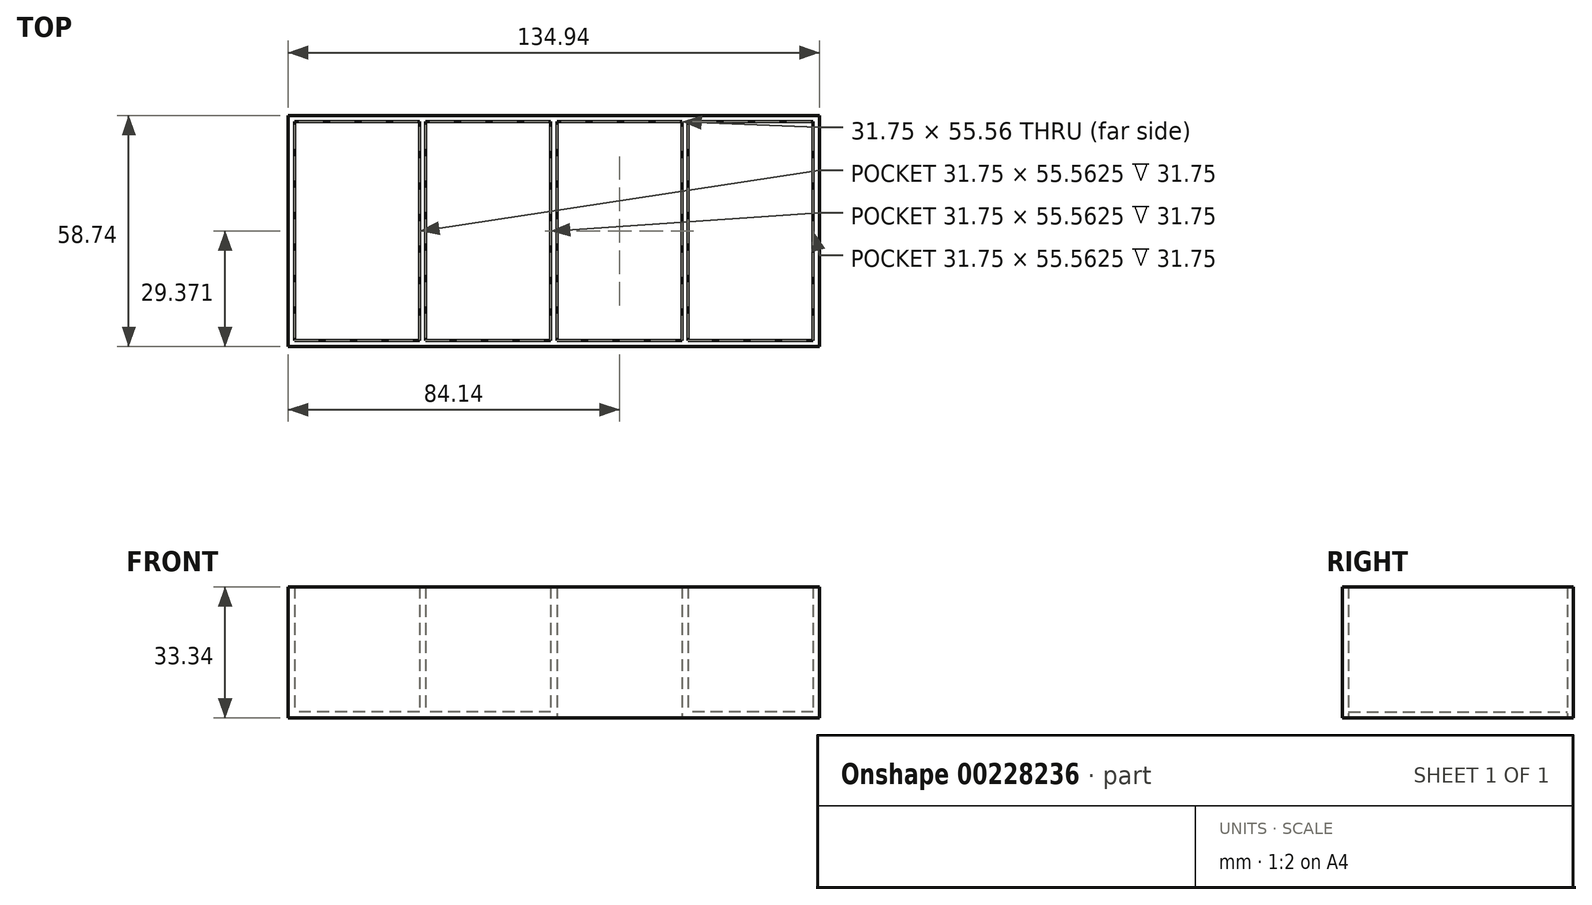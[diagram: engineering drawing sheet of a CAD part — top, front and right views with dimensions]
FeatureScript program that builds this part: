
annotation { "Feature Type Name" : "Feature", "Feature Type Description" : "" }
export const myFeature = defineFeature(function(context is Context, id is Id, definition is map)
    precondition{}
    {
        {
            var Q0;
            Q0=qCreatedBy(makeId("Top.planeOp"),FACE);
            var sketch = newSketch(context, id + "F0", { "sketchPlane" : qUnion([Q0])});
            skLineSegment(sketch, "E0.bottom", {"start": v(0, 0) * mm, "end": v(-31.75, 0) * mm});
            skLineSegment(sketch, "E0.top", {"start": v(0, 55.56) * mm, "end": v(-31.75, 55.56) * mm});
            skLineSegment(sketch, "E0.left", {"start": v(0, 0) * mm, "end": v(0, 55.56) * mm});
            skLineSegment(sketch, "E0.right", {"start": v(-31.75, 0) * mm, "end": v(-31.75, 55.56) * mm});
            skLineSegment(sketch, "E1.bottom", {"start": v(0, 0) * mm, "end": v(1.59, 0) * mm});
            skLineSegment(sketch, "E1.top", {"start": v(0, 55.56) * mm, "end": v(1.59, 55.56) * mm});
            skLineSegment(sketch, "E1.right", {"start": v(1.59, 0) * mm, "end": v(1.59, 55.56) * mm});
            skLineSegment(sketch, "E2.1.0.1", {"start": v(33.34, 55.56) * mm, "end": v(1.59, 55.56) * mm});
            skLineSegment(sketch, "E2.1.0.2", {"start": v(33.34, 0) * mm, "end": v(1.59, 0) * mm});
            skLineSegment(sketch, "E2.1.0.3", {"start": v(33.34, 0) * mm, "end": v(33.34, 55.56) * mm});
            skLineSegment(sketch, "E2.1.0.4", {"start": v(34.93, 0) * mm, "end": v(34.92, 55.56) * mm});
            skLineSegment(sketch, "E2.1.0.5", {"start": v(33.34, 0) * mm, "end": v(34.93, 0) * mm});
            skLineSegment(sketch, "E2.1.0.6", {"start": v(33.34, 55.56) * mm, "end": v(34.92, 55.56) * mm});
            skLineSegment(sketch, "E2.2.0.0", {"start": v(34.93, 0) * mm, "end": v(34.93, 55.56) * mm});
            skLineSegment(sketch, "E2.2.0.1", {"start": v(66.67, 55.56) * mm, "end": v(34.93, 55.56) * mm});
            skLineSegment(sketch, "E2.2.0.2", {"start": v(66.68, 0) * mm, "end": v(34.93, 0) * mm});
            skLineSegment(sketch, "E2.2.0.3", {"start": v(66.68, 0) * mm, "end": v(66.68, 55.56) * mm});
            skLineSegment(sketch, "E2.2.0.4", {"start": v(68.26, 0) * mm, "end": v(68.26, 55.56) * mm});
            skLineSegment(sketch, "E2.2.0.5", {"start": v(66.68, 0) * mm, "end": v(68.26, 0) * mm});
            skLineSegment(sketch, "E2.2.0.6", {"start": v(66.67, 55.56) * mm, "end": v(68.26, 55.56) * mm});
            skLineSegment(sketch, "E2.direction1", {"start": v(-31.75, 0) * mm, "end": v(1.59, 0) * mm, "construction": true});
            skLineSegment(sketch, "E3.3.3.0", {"start": v(100.01, 55.56) * mm, "end": v(68.26, 55.56) * mm});
            skLineSegment(sketch, "E3.6.3.0", {"start": v(100.01, 0) * mm, "end": v(68.26, 0) * mm});
            skLineSegment(sketch, "E3.9.3.0", {"start": v(100.01, 0) * mm, "end": v(100.01, 55.56) * mm});
            skLineSegment(sketch, "E3.12.3.0", {"start": v(101.6, 0) * mm, "end": v(101.6, 55.56) * mm});
            skLineSegment(sketch, "E3.15.3.0", {"start": v(100.01, 0) * mm, "end": v(101.6, 0) * mm});
            skLineSegment(sketch, "E3.18.3.0", {"start": v(100.01, 55.56) * mm, "end": v(101.6, 55.56) * mm});
            skLineSegment(sketch, "E4.bottom", {"start": v(-31.75, 0) * mm, "end": v(-33.34, 0) * mm});
            skLineSegment(sketch, "E4.top", {"start": v(-31.75, 55.56) * mm, "end": v(-33.34, 55.56) * mm});
            skLineSegment(sketch, "E4.right", {"start": v(-33.34, 0) * mm, "end": v(-33.34, 55.56) * mm});
            skLineSegment(sketch, "E5.bottom", {"start": v(-33.34, 55.56) * mm, "end": v(101.6, 55.56) * mm});
            skLineSegment(sketch, "E5.top", {"start": v(-33.34, 57.15) * mm, "end": v(101.6, 57.15) * mm});
            skLineSegment(sketch, "E5.left", {"start": v(-33.34, 55.56) * mm, "end": v(-33.34, 57.15) * mm});
            skLineSegment(sketch, "E5.right", {"start": v(101.6, 55.56) * mm, "end": v(101.6, 57.15) * mm});
            skLineSegment(sketch, "E6.bottom", {"start": v(-33.34, 0) * mm, "end": v(101.6, 0) * mm});
            skLineSegment(sketch, "E6.top", {"start": v(-33.34, -1.59) * mm, "end": v(101.6, -1.59) * mm});
            skLineSegment(sketch, "E6.left", {"start": v(-33.34, 0) * mm, "end": v(-33.34, -1.59) * mm});
            skLineSegment(sketch, "E6.right", {"start": v(101.6, 0) * mm, "end": v(101.6, -1.59) * mm});
            skSolve(sketch);
        }
        {
            var Q0;
            Q0 = qSketchRegion(id + "F0", true);
            var Q1;
            {var subQ0=sQuery(id+"F0.wireOp",EDGE,"E0.left");Q1=makeQuery(id+"F0.imprint","IMPRINT",FACE,{"disambiguationData":[TD([[makeQuery(id+"F0.imprint","IMPRINT",EDGE,{"derivedFrom":subQ0}),-1.0]])]});}
            var Q2;
            {var subQ0=sQuery(id+"F0.wireOp",EDGE,"E2.1.0.3");Q2=makeQuery(id+"F0.imprint","IMPRINT",FACE,{"disambiguationData":[TD([[makeQuery(id+"F0.imprint","IMPRINT",EDGE,{"derivedFrom":subQ0}),-1.0]])]});}
            var Q3;
            {var subQ0=sQuery(id+"F0.wireOp",EDGE,"E2.2.0.3");Q3=makeQuery(id+"F0.imprint","IMPRINT",FACE,{"disambiguationData":[TD([[makeQuery(id+"F0.imprint","IMPRINT",EDGE,{"derivedFrom":subQ0}),-1.0]])]});}
            extrude(context, id + "F1", {"entities" : qUnion([Q0, Q1, Q2, Q3]), "depth" : 33.34 * mm});
        }
        {
            var Q0;
            {var subQ0=sQuery(id+"F0.wireOp",EDGE,"E0.left");Q0=makeQuery(id+"F0.imprint","IMPRINT",FACE,{"disambiguationData":[TD([[makeQuery(id+"F0.imprint","IMPRINT",EDGE,{"derivedFrom":subQ0}),1.0]])]});}
            var Q1;
            {var subQ0=sQuery(id+"F0.wireOp",EDGE,"E1.right");Q1=makeQuery(id+"F0.imprint","IMPRINT",FACE,{"disambiguationData":[TD([[makeQuery(id+"F0.imprint","IMPRINT",EDGE,{"derivedFrom":subQ0}),-1.0]])]});}
            var Q2;
            {var subQ0=sQuery(id+"F0.wireOp",EDGE,"E2.2.0.4");Q2=makeQuery(id+"F0.imprint","IMPRINT",FACE,{"disambiguationData":[TD([[makeQuery(id+"F0.imprint","IMPRINT",EDGE,{"derivedFrom":subQ0}),-1.0]])]});}
            var Q3;
            {var subQ0=sQuery(id+"F0.wireOp",EDGE,"E2.2.0.0");Q3=makeQuery(id+"F0.imprint","IMPRINT",FACE,{"disambiguationData":[TD([[makeQuery(id+"F0.imprint","IMPRINT",EDGE,{"derivedFrom":subQ0}),-1.0]])]});}
            extrude(context, id + "F2", {"entities" : qUnion([Q0, Q1, Q2, Q3]), "operationType" : NewBodyOperationType.ADD, "depth" : 1.59 * mm});
        }
    });
